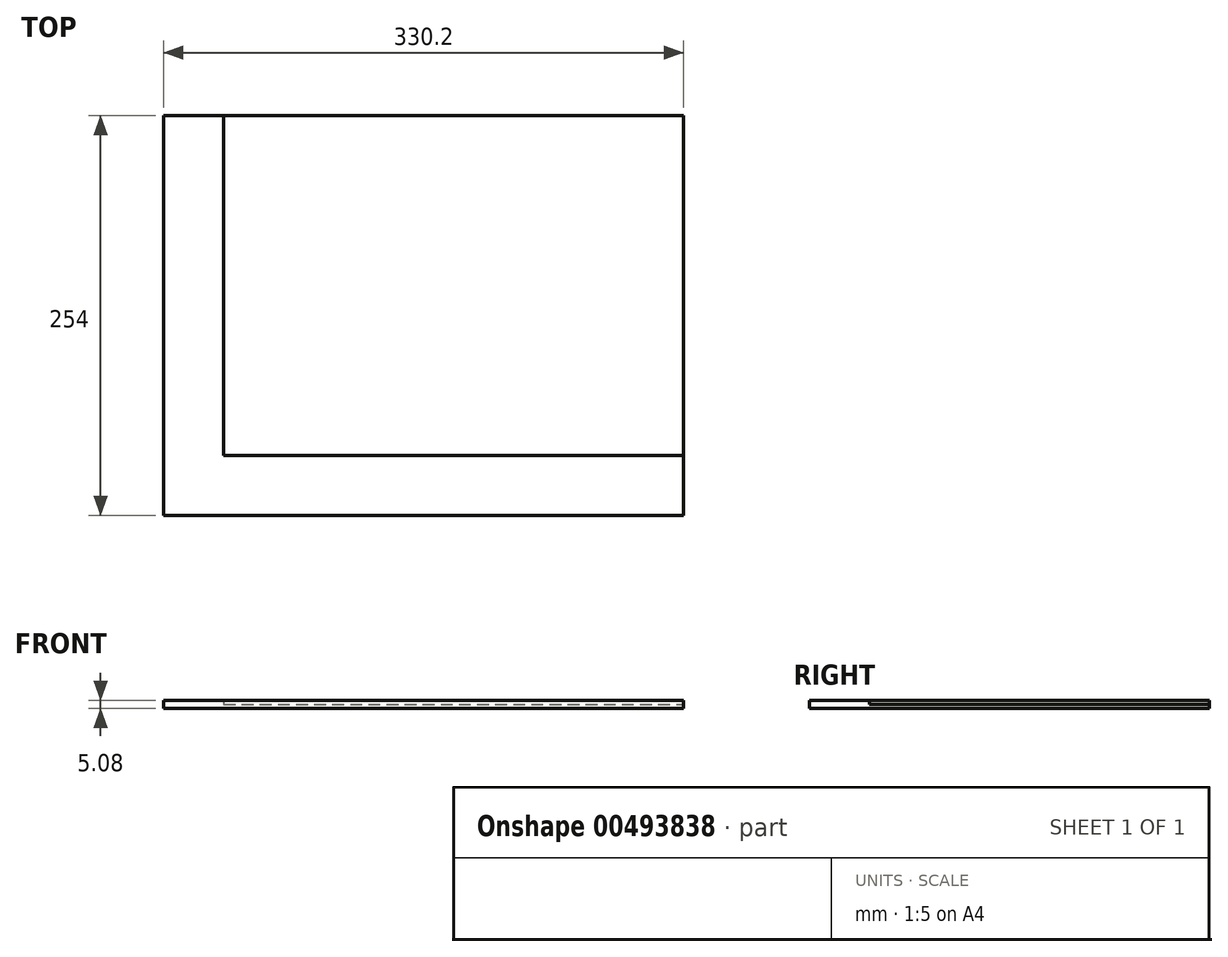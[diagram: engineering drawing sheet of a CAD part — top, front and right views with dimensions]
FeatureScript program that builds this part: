
annotation { "Feature Type Name" : "Feature", "Feature Type Description" : "" }
export const myFeature = defineFeature(function(context is Context, id is Id, definition is map)
    precondition{}
    {
        {
            var Q0;
            Q0=qCreatedBy(makeId("Top.planeOp"),FACE);
            var sketch = newSketch(context, id + "F0", { "sketchPlane" : qUnion([Q0])});
            skLineSegment(sketch, "E0.bottom", {"start": v(-163.58, 186.8) * mm, "end": v(166.62, 186.8) * mm});
            skLineSegment(sketch, "E0.top", {"start": v(-163.58, -67.2) * mm, "end": v(166.62, -67.2) * mm});
            skLineSegment(sketch, "E0.left", {"start": v(-163.58, 186.8) * mm, "end": v(-163.58, -67.2) * mm});
            skLineSegment(sketch, "E0.right", {"start": v(166.62, 186.8) * mm, "end": v(166.62, -67.2) * mm});
            skLineSegment(sketch, "E1.top", {"start": v(-163.58, -29.1) * mm, "end": v(166.62, -29.1) * mm});
            skLineSegment(sketch, "E1.left", {"start": v(-163.58, -67.2) * mm, "end": v(-163.58, -29.1) * mm});
            skLineSegment(sketch, "E1.right", {"start": v(166.62, -67.2) * mm, "end": v(166.62, -29.1) * mm});
            skLineSegment(sketch, "E2.bottom", {"start": v(-163.58, 186.8) * mm, "end": v(-125.48, 186.8) * mm});
            skLineSegment(sketch, "E2.top", {"start": v(-163.58, -29.1) * mm, "end": v(-125.48, -29.1) * mm});
            skLineSegment(sketch, "E2.left", {"start": v(-163.58, 186.8) * mm, "end": v(-163.58, -29.1) * mm});
            skLineSegment(sketch, "E2.right", {"start": v(-125.48, 186.8) * mm, "end": v(-125.48, -29.1) * mm});
            skSolve(sketch);
        }
        {
            var Q0;
            Q0=makeQuery(id+"F0.imprint","IMPRINT",FACE,{"disambiguationData":[TD([[makeQuery(id+"F0.imprint","IMPRINT",EDGE,{"derivedFrom":sQuery(id+"F0.wireOp",EDGE,"E0.bottom")}),-1.0]])]});
            var Q1;
            Q1=makeQuery(id+"F0.imprint","IMPRINT",FACE,{"disambiguationData":[TD([[makeQuery(id+"F0.imprint","IMPRINT",EDGE,{"derivedFrom":sQuery(id+"F0.wireOp",EDGE,"E2.bottom")}),-1.0]])]});
            var Q2;
            Q2=makeQuery(id+"F0.imprint","IMPRINT",FACE,{"disambiguationData":[TD([[makeQuery(id+"F0.imprint","IMPRINT",EDGE,{"derivedFrom":sQuery(id+"F0.wireOp",EDGE,"E0.top")}),1.0]])]});
            extrude(context, id + "F1", {"entities" : qUnion([Q0, Q1, Q2]), "depth" : 2.54 * mm});
        }
        {
            var Q0;
            Q0=makeQuery(id+"F1.opExtrude","CAP_FACE",FACE,{"disambiguationData":[OSD([sQuery(id+"F0.wireOp",EDGE,"E0.bottom"),sQuery(id+"F0.wireOp",EDGE,"E0.right"),sQuery(id+"F0.wireOp",EDGE,"E0.top"),sQuery(id+"F0.wireOp",EDGE,"E1.left"),sQuery(id+"F0.wireOp",EDGE,"E1.right"),sQuery(id+"F0.wireOp",EDGE,"E2.bottom"),sQuery(id+"F0.wireOp",EDGE,"E2.left")])],"isStart":false});
            var sketch = newSketch(context, id + "F2", { "sketchPlane" : qUnion([Q0])});
            skLineSegment(sketch, "E3.bottom", {"start": v(-163.58, 186.8) * mm, "end": v(-125.48, 186.8) * mm});
            skLineSegment(sketch, "E3.top", {"start": v(-163.58, -67.2) * mm, "end": v(-125.48, -67.2) * mm});
            skLineSegment(sketch, "E3.left", {"start": v(-163.58, 186.8) * mm, "end": v(-163.58, -67.2) * mm});
            skLineSegment(sketch, "E3.right", {"start": v(-125.48, 186.8) * mm, "end": v(-125.48, -67.2) * mm});
            skLineSegment(sketch, "E4.bottom", {"start": v(-125.48, -67.2) * mm, "end": v(166.62, -67.2) * mm});
            skLineSegment(sketch, "E4.top", {"start": v(-125.48, -29.1) * mm, "end": v(166.62, -29.1) * mm});
            skLineSegment(sketch, "E4.left", {"start": v(-125.48, -67.2) * mm, "end": v(-125.48, -29.1) * mm});
            skLineSegment(sketch, "E4.right", {"start": v(166.62, -67.2) * mm, "end": v(166.62, -29.1) * mm});
            skSolve(sketch);
        }
        {
            var Q0;
            Q0=makeQuery(id+"F2.imprint","IMPRINT",FACE,{"disambiguationData":[TD([[makeQuery(id+"F2.imprint","IMPRINT",EDGE,{"derivedFrom":sQuery(id+"F2.wireOp",EDGE,"E4.bottom")}),1.0]])]});
            var Q1;
            Q1=makeQuery(id+"F2.imprint","IMPRINT",FACE,{"disambiguationData":[TD([[makeQuery(id+"F2.imprint","IMPRINT",EDGE,{"derivedFrom":sQuery(id+"F2.wireOp",EDGE,"E3.bottom")}),-1.0]])]});
            extrude(context, id + "F3", {"entities" : qUnion([Q0, Q1]), "operationType" : NewBodyOperationType.ADD, "depth" : 2.54 * mm});
        }
    });
